# Revit family: KingswayGroup_PllHndls_ClassicGripAnti-LigatureHandleOnBackPlate
name_source: partatom
category: Specialty Equipment
units: mm (PartAtom-declared; Revit-internal decimal feet)

## family parameters
Always vertical = Yes
Cut with Voids When Loaded = No
Part Type = Normal
Room Calculation Point = No
Round Connector Dimension = Use Diameter
Shared = No
Work Plane-Based = No

## types (1)
- KingswayGroup_PllHndls_ClassicGripAnti-LigatureHandleOnBackPlate
    AssetType = Fixed
    BIMObjectName = KingswayGroup_PullHandles_ClassicGripAnti-LigatureHandleOnBackPlate
    Category = Pr_30_36_59_64:Pull handles
    Color = For full range of available finishes and colours, contact Kingsway Group
    Default Elevation = 0 mm  [stored 0 ft]
    Description = Classic Grip Pull Handle On Backplate
    DurationUnit = year
    Features = A solid anti-ligature handle with a large finger grip area to aid those with impaired manual dexterity. The handle is supplied on a large chamfered finger plate with radiused ends and countersunk fixing holes.
    Finish = For full range of available finishes and colours, contact Kingsway Group
    IfcExportAs = IfcDiscreteAccessoryType
    IfcExportType = USERDEFINED
    Manufacturer = Kingsway Group
    ManufacturerName = Kingsway Group
    ManufacturerURL = https://kingswaygroupglobal.com
    Material = For full range of available material, contact Kingsway Group
    Model = KG60
    ModelNumber = KG60
    ModelReference = Classic GripAnti-Ligature Handle (On Backplate)
    Name = PullHandles_ClassicGripAnti-LigatureHandleOnBackPlate_KG60_KingswayGroup
    NominalHeight = 270 mm  [stored 0.885827 ft]
    NominalLength = 70 mm  [stored 0.229659 ft]
    NominalWidth = 47.8 mm  [stored 0.156824 ft]
    ProductInformation = https://kingswaygroupglobal.com
    Size = 70 x 270 x 47.8 mm
    URL = https://kingswaygroupglobal.com
    Uniclass2015Code = Pr_30_36_59_64
    Uniclass2015Title = Pull handles
    Uniclass2015Version = Products v1.36
    Version = 1
    WarrantyDescription = 5-Year Guarantee *For faulty manufacture and not for damage
    WarrantyDurationParts = 5
    WarrantyDurationUnit = year

note: [stored X ft] marks values corroborated as IEEE doubles in the binary element streams (Revit-internal decimal feet)

## geometry (parser evidence)
native form markers: Sweep x2
no freeform markers — native parametric forms only
